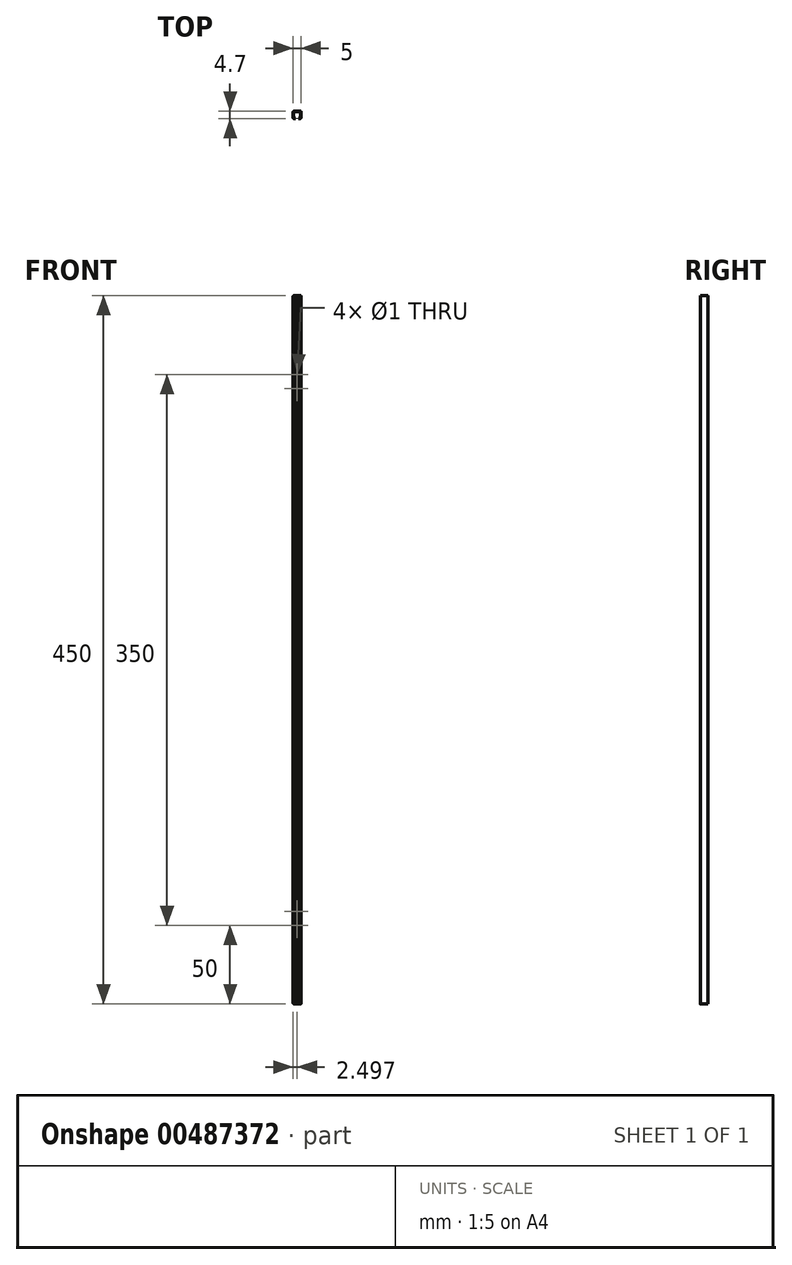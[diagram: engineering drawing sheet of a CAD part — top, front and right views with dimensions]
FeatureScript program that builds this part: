
annotation { "Feature Type Name" : "Feature", "Feature Type Description" : "" }
export const myFeature = defineFeature(function(context is Context, id is Id, definition is map)
    precondition{}
    {
        {
            var Q0;
            Q0=qCreatedBy(makeId("Top.planeOp"),FACE);
            var sketch = newSketch(context, id + "F0", { "sketchPlane" : qUnion([Q0])});
            skLineSegment(sketch, "E0", {"start": v(-1.6, 0) * mm, "end": v(-3.1, 0) * mm});
            skLineSegment(sketch, "E1", {"start": v(-3.1, 0) * mm, "end": v(-3.1, 4.7) * mm});
            skLineSegment(sketch, "E2", {"start": v(-3.1, 4.7) * mm, "end": v(1.9, 4.7) * mm});
            skLineSegment(sketch, "E3", {"start": v(1.9, 4.7) * mm, "end": v(1.9, 0) * mm});
            skLineSegment(sketch, "E4", {"start": v(1.9, 0) * mm, "end": v(0.4, 0) * mm});
            skLineSegment(sketch, "E5", {"start": v(-1.6, 0.3) * mm, "end": v(-2.8, 0.3) * mm});
            skLineSegment(sketch, "E6", {"start": v(-2.8, 0.3) * mm, "end": v(-2.8, 4.4) * mm});
            skLineSegment(sketch, "E7", {"start": v(-2.8, 4.4) * mm, "end": v(1.6, 4.4) * mm});
            skLineSegment(sketch, "E8", {"start": v(1.6, 4.4) * mm, "end": v(1.6, 0.3) * mm});
            skLineSegment(sketch, "E9", {"start": v(1.6, 0.3) * mm, "end": v(0.4, 0.3) * mm});
            skLineSegment(sketch, "E10", {"start": v(0.4, 0) * mm, "end": v(0.4, 0.3) * mm});
            skLineSegment(sketch, "E11", {"start": v(-1.6, 0) * mm, "end": v(-1.6, 0.3) * mm});
            skSolve(sketch);
        }
        {
            var Q0;
            Q0 = qSketchRegion(id + "F0", true);
            extrude(context, id + "F1", {"entities" : qUnion([Q0]), "depth" : 450 * mm});
        }
        {
            var Q0;
            Q0=makeQuery(id+"F1.opExtrude","SWEPT_FACE",FACE,{"disambiguationData":[OSD([sQuery(id+"F0.wireOp",EDGE,"E1")])]});
            var Q1;
            Q1=makeQuery(id+"F1.opExtrude","SWEPT_EDGE",EDGE,{"disambiguationData":[OSD([sQuery(id+"F0.wireOp",EDGE,"E0"),sQuery(id+"F0.wireOp",EDGE,"E1")])]});
            var Q2;
            Q2=makeQuery(id+"F1.opExtrude","SWEPT_FACE",FACE,{"disambiguationData":[OSD([sQuery(id+"F0.wireOp",EDGE,"E3")])]});
            fillet(context, id + "F2", {"entities" : qUnion([Q0, Q1, Q2]), "radius" : 0.5 * mm, "tangentPropagation" : true, "allowEdgeOverflow" : false});
        }
        {
            var Q0;
            Q0=makeQuery(id+"F1.opExtrude","SWEPT_FACE",FACE,{"disambiguationData":[OSD([sQuery(id+"F0.wireOp",EDGE,"E2")])]});
            var sketch = newSketch(context, id + "F3", { "sketchPlane" : qUnion([Q0])});
            skCircle(sketch, "E12", {"center": v(0.6, 400) * mm, "radius": 0.5 * mm});
            skCircle(sketch, "E13", {"center": v(0.6, 391) * mm, "radius": 0.5 * mm});
            skCircle(sketch, "E14", {"center": v(0.6, 50) * mm, "radius": 0.5 * mm});
            skCircle(sketch, "E15", {"center": v(0.6, 59) * mm, "radius": 0.5 * mm});
            skSolve(sketch);
        }
        {
            var Q0;
            Q0 = qSketchRegion(id + "F3", true);
            extrude(context, id + "F4", {"entities" : qUnion([Q0]), "operationType" : NewBodyOperationType.REMOVE, "oppositeDirection" : true, "depth" : 25 * mm});
        }
    });
